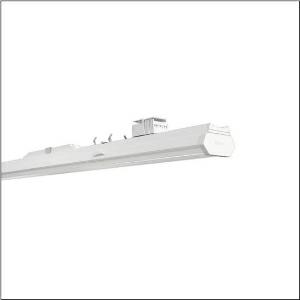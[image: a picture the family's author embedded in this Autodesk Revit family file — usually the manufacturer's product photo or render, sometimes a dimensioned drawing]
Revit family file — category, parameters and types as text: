
# Revit family: licross_r__11_protected_extreme_ho_51tp12dn6e5me_8bd9
name_source: partatom
category: Lighting Fixtures
units: mm (PartAtom-declared; Revit-internal decimal feet)

## family parameters
Cut with Voids When Loaded = No
Host = Face
Light Source = No
Part Type = Normal
Room Calculation Point = No
Round Connector Dimension = Use Diameter
Shared = No

## types (1)
- --- (1 x LED, 14910 lm, 87.3 W, 6500K)
    Apparent Load = 87 VA
    CIE Flux Codes = 70 91 97 98 100
    Color Rendering = 80
    Color Temperature = 6500K
    Default Elevation = 1800 mm
    Description = Licross® 11 Protected extreme HO, luminaire insert, of sheet steel, galvanised, coil coated, white, length: 1.500mm, width: 90mm, height: 101mm, LED rated luminous flux: 14.910lm, light colour: 865, control gear: DALI 2, with plug, 5-pole, with phase selection, mains connection: 220..240V, AC, 50/60Hz, rated input power: 87W, internal wiring halogen-free, primary optical cover: cover, of PMMA, light emission: direct distribution, primary light characteristic: symmetric, protection rating (complete): IP64, insulation class (complete): insulation class I (protective earthing), certification: CE, ENEC, VDE, UKCA, protection symbol: D if used in an environment with conductive dust loads with corresponding accessories, impact resistance: IK06, permissible ambient temperature for indoor applications: -40..+40°C, LABS conformity tested according to VDMA 24364:2018-05, reducing of maximum allowable ambient temperature of 5°C with ceiling mounting, corresponds to IFS (International Featured Standards) requirements for safety and quality in the food industry, packaging unit: 1 piece
    Height = 92 mm
    Lamp = 1 x LED
    Lamp Light Flux = 14910 lm
    Lamp Power = 87.3 W
    Lamp count = 1
    Length = 1500 mm
    Luminous efficacy = 171 lm/W
    Manufacturer = Siteco
    ModVariant = No
    Model = 51TP12DN6E5ME
    Mounting Place = Ceiling
    Mounting Type = Pendant
    Number of Poles = 1
    OnlyDefault = Yes
    Power Factor = 1
    Product Name = Licross® 11 Protected extreme HO
    Product group = luminaire insert | ceiling pendant
    ProductGroupID = 902
    Protection Class = Protection class I
    Protection Degree = IP 64
    RLX_Detail_Level = 1
    RLX_Emergency_Light_Flux = 0 lm
    RLX_Emergency_Type = 0
    RLX_Emergency_Type_DB = No
    RlxData = <blob elided: 24477 chars, md5=fc30b739>
    Socket = socket
    Standby Power = 0 W
    System Light Flux = 14910 lm
    System Power = 87 W
    Type Comments = factory setting: luminous flux: 100 % | dim-lin: 254 | 589 mA
    Type Image = l_1256148.jpg
    URL = http://relux.com
    VarID = @adj_030381
    Voltage = 0 V
    Weight = 0.00 kg
    Width = 88 mm

## geometry (parser evidence)
native form markers: Blend x4, Sweep x12
no freeform markers — native parametric forms only
